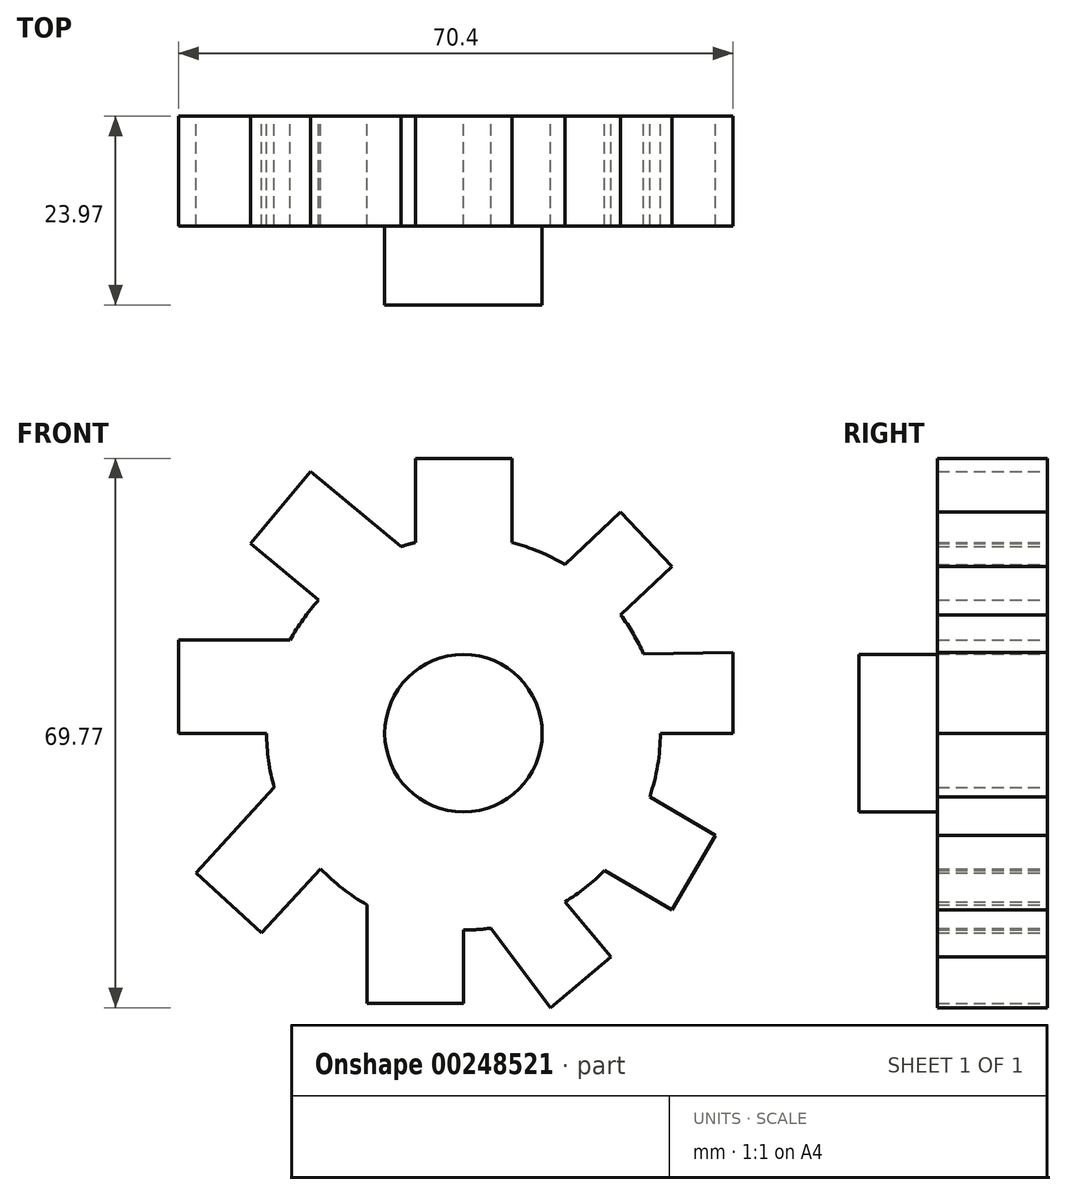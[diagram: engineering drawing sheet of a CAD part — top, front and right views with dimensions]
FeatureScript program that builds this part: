
annotation { "Feature Type Name" : "Feature", "Feature Type Description" : "" }
export const myFeature = defineFeature(function(context is Context, id is Id, definition is map)
    precondition{}
    {
        {
            var Q0;
            Q0=qCreatedBy(makeId("Front.planeOp"),FACE);
            var sketch = newSketch(context, id + "F0", { "sketchPlane" : qUnion([Q0])});
            skArc(sketch, "E0", {"start": v(-18.41, 16.91) * mm, "mid": v(-20.38, 14.48) * mm, "end": v(-22.02, 11.83) * mm});
            skLineSegment(sketch, "E1", {"start": v(-6.06, 24.25) * mm, "end": v(-6.06, 34.9) * mm});
            skLineSegment(sketch, "E2", {"start": v(-6.06, 34.9) * mm, "end": v(6.18, 34.9) * mm});
            skLineSegment(sketch, "E3", {"start": v(6.18, 34.9) * mm, "end": v(6.18, 24.22) * mm});
            skLineSegment(sketch, "E4", {"start": v(12.87, 21.44) * mm, "end": v(19.97, 28.1) * mm});
            skLineSegment(sketch, "E5", {"start": v(19.97, 28.1) * mm, "end": v(26.49, 21.16) * mm});
            skLineSegment(sketch, "E6", {"start": v(26.49, 21.16) * mm, "end": v(19.97, 15.04) * mm});
            skLineSegment(sketch, "E7", {"start": v(22.89, 10.06) * mm, "end": v(34.22, 10.29) * mm});
            skLineSegment(sketch, "E8", {"start": v(34.22, 10.29) * mm, "end": v(34.22, 0) * mm});
            skLineSegment(sketch, "E9", {"start": v(34.22, 0) * mm, "end": v(25, 0) * mm});
            skLineSegment(sketch, "E10", {"start": v(23.66, -8.07) * mm, "end": v(32.03, -12.96) * mm});
            skLineSegment(sketch, "E11", {"start": v(32.03, -12.96) * mm, "end": v(26.48, -22.46) * mm});
            skLineSegment(sketch, "E12", {"start": v(26.48, -22.46) * mm, "end": v(17.9, -17.45) * mm});
            skLineSegment(sketch, "E13", {"start": v(12.87, -21.43) * mm, "end": v(18.73, -28.4) * mm});
            skLineSegment(sketch, "E14", {"start": v(18.73, -28.4) * mm, "end": v(11.04, -34.86) * mm});
            skLineSegment(sketch, "E15", {"start": v(11.04, -34.86) * mm, "end": v(3.48, -24.76) * mm});
            skLineSegment(sketch, "E16", {"start": v(0, -25) * mm, "end": v(0, -34.33) * mm});
            skLineSegment(sketch, "E17", {"start": v(0, -34.33) * mm, "end": v(-12.23, -34.33) * mm});
            skLineSegment(sketch, "E18", {"start": v(-12.23, -34.33) * mm, "end": v(-12.23, -21.8) * mm});
            skLineSegment(sketch, "E19", {"start": v(-18.14, -17.2) * mm, "end": v(-25.62, -25.36) * mm});
            skLineSegment(sketch, "E20", {"start": v(-25.62, -25.36) * mm, "end": v(-33.95, -17.72) * mm});
            skLineSegment(sketch, "E21", {"start": v(-33.95, -17.72) * mm, "end": v(-24.03, -6.9) * mm});
            skLineSegment(sketch, "E22", {"start": v(-25, 0) * mm, "end": v(-36.18, 0) * mm});
            skLineSegment(sketch, "E23", {"start": v(-36.18, 0) * mm, "end": v(-36.18, 11.83) * mm});
            skLineSegment(sketch, "E24", {"start": v(-36.18, 11.83) * mm, "end": v(-22.02, 11.83) * mm});
            skLineSegment(sketch, "E25", {"start": v(-18.41, 16.91) * mm, "end": v(-27.04, 24.09) * mm});
            skLineSegment(sketch, "E26", {"start": v(-27.04, 24.09) * mm, "end": v(-19.44, 33.23) * mm});
            skLineSegment(sketch, "E27", {"start": v(-19.44, 33.23) * mm, "end": v(-7.97, 23.7) * mm});
            skArc(sketch, "E28.trimOffspring", {"start": v(-6.06, 24.25) * mm, "mid": v(-7.02, 24) * mm, "end": v(-7.97, 23.7) * mm});
            skArc(sketch, "E29.trimOffspring", {"start": v(12.87, 21.44) * mm, "mid": v(9.62, 23.07) * mm, "end": v(6.18, 24.22) * mm});
            skArc(sketch, "E30.trimOffspring", {"start": v(22.89, 10.06) * mm, "mid": v(21.57, 12.64) * mm, "end": v(19.97, 15.04) * mm});
            skArc(sketch, "E31.trimOffspring", {"start": v(23.66, -8.07) * mm, "mid": v(24.66, -4.1) * mm, "end": v(25, 0) * mm});
            skArc(sketch, "E32.trimOffspring", {"start": v(12.87, -21.43) * mm, "mid": v(15.52, -19.6) * mm, "end": v(17.9, -17.45) * mm});
            skArc(sketch, "E33.trimOffspring", {"start": v(0, -25) * mm, "mid": v(1.74, -24.94) * mm, "end": v(3.48, -24.76) * mm});
            skArc(sketch, "E34.trimOffspring", {"start": v(-18.14, -17.2) * mm, "mid": v(-15.36, -19.73) * mm, "end": v(-12.23, -21.8) * mm});
            skArc(sketch, "E35.trimOffspring", {"start": v(-25, 0) * mm, "mid": v(-24.76, -3.48) * mm, "end": v(-24.03, -6.9) * mm});
            skSolve(sketch);
        }
        {
            var Q0;
            Q0=makeQuery(id+"F0.imprint","IMPRINT",FACE,{"disambiguationData":[TD([[makeQuery(id+"F0.imprint","IMPRINT",EDGE,{"derivedFrom":sQuery(id+"F0.wireOp",EDGE,"E0")}),1.0]])]});
            extrude(context, id + "F1", {"entities" : qUnion([Q0]), "depth" : 13.97 * mm});
        }
        {
            var Q0;
            Q0=makeQuery(id+"F1.opExtrude","CAP_FACE",FACE,{"disambiguationData":[OSD([sQuery(id+"F0.wireOp",EDGE,"E0"),sQuery(id+"F0.wireOp",EDGE,"E1"),sQuery(id+"F0.wireOp",EDGE,"E2"),sQuery(id+"F0.wireOp",EDGE,"E3"),sQuery(id+"F0.wireOp",EDGE,"E4"),sQuery(id+"F0.wireOp",EDGE,"E5"),sQuery(id+"F0.wireOp",EDGE,"E6"),sQuery(id+"F0.wireOp",EDGE,"E7"),sQuery(id+"F0.wireOp",EDGE,"E8"),sQuery(id+"F0.wireOp",EDGE,"E9"),sQuery(id+"F0.wireOp",EDGE,"E10"),sQuery(id+"F0.wireOp",EDGE,"E11"),sQuery(id+"F0.wireOp",EDGE,"E12"),sQuery(id+"F0.wireOp",EDGE,"E13"),sQuery(id+"F0.wireOp",EDGE,"E14"),sQuery(id+"F0.wireOp",EDGE,"E15"),sQuery(id+"F0.wireOp",EDGE,"E16"),sQuery(id+"F0.wireOp",EDGE,"E17"),sQuery(id+"F0.wireOp",EDGE,"E18"),sQuery(id+"F0.wireOp",EDGE,"E19"),sQuery(id+"F0.wireOp",EDGE,"E20"),sQuery(id+"F0.wireOp",EDGE,"E21"),sQuery(id+"F0.wireOp",EDGE,"E22"),sQuery(id+"F0.wireOp",EDGE,"E23"),sQuery(id+"F0.wireOp",EDGE,"E24"),sQuery(id+"F0.wireOp",EDGE,"E25"),sQuery(id+"F0.wireOp",EDGE,"E26"),sQuery(id+"F0.wireOp",EDGE,"E27"),sQuery(id+"F0.wireOp",EDGE,"E28.trimOffspring"),sQuery(id+"F0.wireOp",EDGE,"E29.trimOffspring"),sQuery(id+"F0.wireOp",EDGE,"E30.trimOffspring"),sQuery(id+"F0.wireOp",EDGE,"E31.trimOffspring"),sQuery(id+"F0.wireOp",EDGE,"E32.trimOffspring"),sQuery(id+"F0.wireOp",EDGE,"E33.trimOffspring"),sQuery(id+"F0.wireOp",EDGE,"E34.trimOffspring"),sQuery(id+"F0.wireOp",EDGE,"E35.trimOffspring")])],"isStart":false});
            var sketch = newSketch(context, id + "F2", { "sketchPlane" : qUnion([Q0])});
            skCircle(sketch, "E36", {"center": v(0, 0) * mm, "radius": 10 * mm});
            skSolve(sketch);
        }
        {
            var Q0;
            Q0=makeQuery(id+"F2.imprint","IMPRINT",FACE,{"disambiguationData":[TD([[makeQuery(id+"F2.imprint","IMPRINT",EDGE,{"derivedFrom":sQuery(id+"F2.wireOp",EDGE,"E36")}),1.0]])]});
            var Q1;
            Q1 = qSketchRegion(id + "F2", true);
            var Q2;
            Q2=sQuery(id+"F2.wireOp",EDGE,"E36");
            extrude(context, id + "F3", {"entities" : qUnion([Q0, Q1]), "operationType" : NewBodyOperationType.ADD, "surfaceEntities" : qUnion([Q2]), "depth" : 10 * mm});
        }
    });
